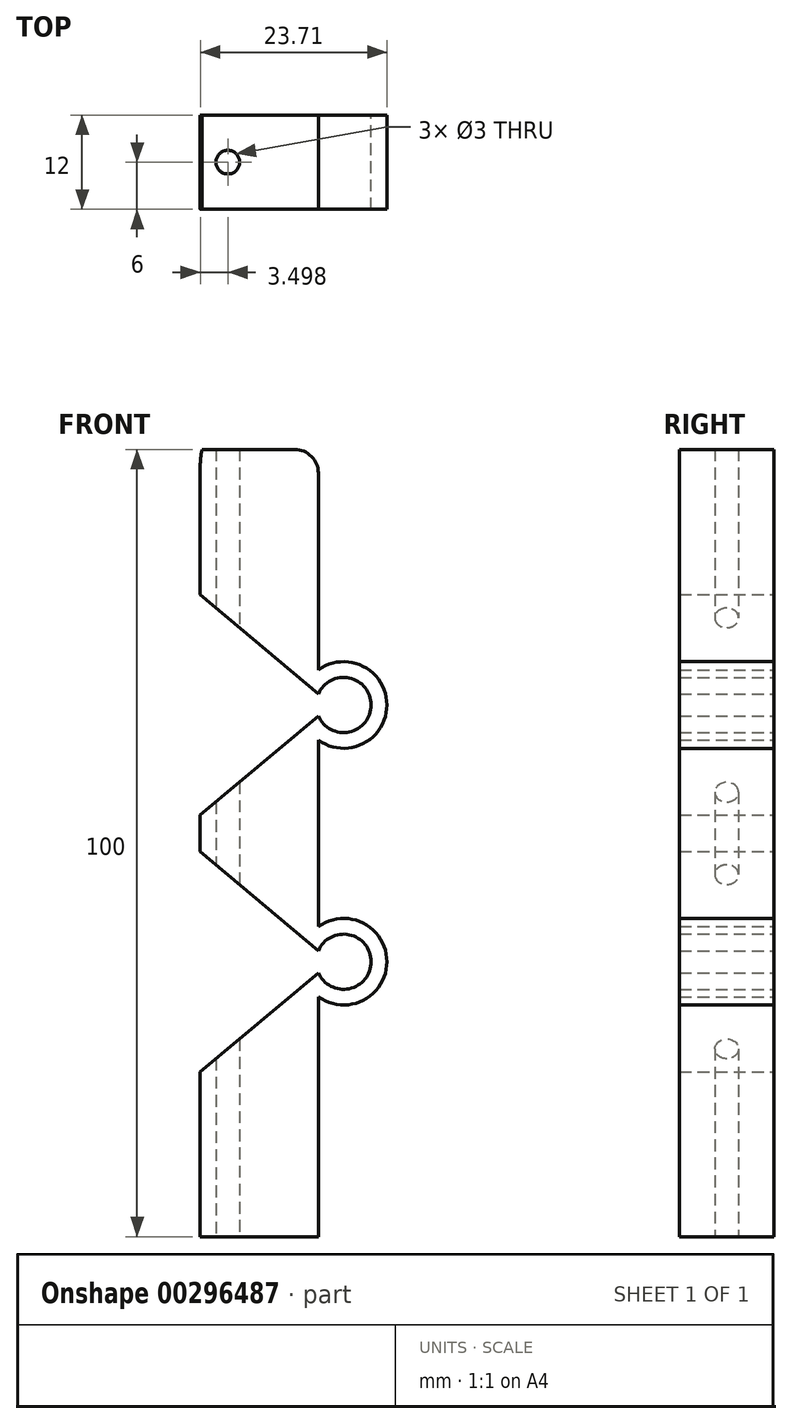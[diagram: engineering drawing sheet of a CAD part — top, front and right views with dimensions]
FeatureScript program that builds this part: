
annotation { "Feature Type Name" : "Feature", "Feature Type Description" : "" }
export const myFeature = defineFeature(function(context is Context, id is Id, definition is map)
    precondition{}
    {
        {
            var Q0;
            Q0=qCreatedBy(makeId("Front.planeOp"),FACE);
            var sketch = newSketch(context, id + "F0", { "sketchPlane" : qUnion([Q0])});
            skLineSegment(sketch, "E0.bottom", {"start": v(-29.07, 0) * mm, "end": v(-44.07, 0) * mm});
            skLineSegment(sketch, "E0.top", {"start": v(-32.07, 100) * mm, "end": v(-43.85, 100) * mm});
            skLineSegment(sketch, "E0.left", {"start": v(-29.07, 0) * mm, "end": v(-29.07, 30.46) * mm});
            skLineSegment(sketch, "E0.right", {"start": v(-44.07, 0) * mm, "end": v(-44.07, 20.92) * mm});
            skLineSegment(sketch, "E1", {"start": v(-29.07, 34.93) * mm, "end": v(-44.07, 34.93) * mm, "construction": true});
            skLineSegment(sketch, "E2", {"start": v(-29.07, 67.54) * mm, "end": v(-44.07, 67.54) * mm, "construction": true});
            skLineSegment(sketch, "E3.trimOffspring", {"start": v(-44.07, 48.93) * mm, "end": v(-44.07, 53.54) * mm});
            skLineSegment(sketch, "E4.trimOffspring", {"start": v(-44.07, 81.55) * mm, "end": v(-44.07, 97.92) * mm});
            skArc(sketch, "E5", {"start": v(-29.36, 35.13) * mm, "mid": v(-29.36, 35.03) * mm, "end": v(-29.36, 34.93) * mm});
            skPoint(sketch, "E5.third.point", {"position": v(-22.36, 34.93) * mm});
            skArc(sketch, "E6", {"start": v(-29.07, 66.14) * mm, "mid": v(-22.36, 67.54) * mm, "end": v(-29.07, 68.94) * mm});
            skPoint(sketch, "E6.third.point", {"position": v(-22.36, 67.54) * mm});
            skArc(sketch, "E7", {"start": v(-29.07, 63.08) * mm, "mid": v(-20.36, 67.54) * mm, "end": v(-29.07, 72.01) * mm});
            skPoint(sketch, "E8.end.orphan", {"position": v(-29.07, 66.14) * mm});
            skPoint(sketch, "E9.MirrorCS.start.orphan", {"position": v(-29.07, 67.54) * mm});
            skLineSegment(sketch, "E10.trimOffspring", {"start": v(-29.07, 72.01) * mm, "end": v(-29.07, 97) * mm});
            skPoint(sketch, "E11.MirrorCS.start.orphan", {"position": v(-29.07, 34.93) * mm});
            skArc(sketch, "E12.trimOffspring", {"start": v(-29.07, 33.53) * mm, "mid": v(-22.36, 34.93) * mm, "end": v(-29.07, 36.33) * mm});
            skLineSegment(sketch, "E13.trimOffspring", {"start": v(-29.07, 39.4) * mm, "end": v(-29.07, 63.08) * mm});
            skArc(sketch, "E14", {"start": v(-29.07, 39.4) * mm, "mid": v(-20.36, 34.93) * mm, "end": v(-29.07, 30.46) * mm});
            skPoint(sketch, "E15.newPointB", {"position": v(-44.07, 100.16) * mm});
            skArc(sketch, "E15.filletArc", {"start": v(-34.07, 107.92) * mm, "mid": v(-41.14, 104.99) * mm, "end": v(-44.07, 97.92) * mm});
            skPoint(sketch, "E16.visualSharp", {"position": v(-29.07, 100) * mm});
            skArc(sketch, "E16.filletArc", {"start": v(-29.07, 97) * mm, "mid": v(-29.95, 99.12) * mm, "end": v(-32.07, 100) * mm});
            skPoint(sketch, "E17.MirrorCS.end.orphan", {"position": v(-44.07, 114.16) * mm});
            skPoint(sketch, "E17.MirrorCS.start.orphan", {"position": v(-29.07, 100.16) * mm});
            skLineSegment(sketch, "E18", {"start": v(-44.07, 48.93) * mm, "end": v(-29.07, 36.33) * mm});
            skLineSegment(sketch, "E19", {"start": v(-44.07, 20.92) * mm, "end": v(-29.07, 33.53) * mm});
            skPoint(sketch, "E20.trimOffspring.start.orphan", {"position": v(-31.07, 36.33) * mm});
            skPoint(sketch, "E21.start.orphan", {"position": v(-31.07, 33.53) * mm});
            skLineSegment(sketch, "E22", {"start": v(-44.07, 81.55) * mm, "end": v(-29.07, 68.94) * mm});
            skLineSegment(sketch, "E23", {"start": v(-29.07, 66.14) * mm, "end": v(-44.07, 53.54) * mm});
            skPoint(sketch, "E24.start.orphan", {"position": v(-31.07, 66.14) * mm});
            skPoint(sketch, "E25.trimOffspring.start.orphan", {"position": v(-31.07, 68.94) * mm});
            skSolve(sketch);
        }
        {
            var Q0;
            Q0=makeQuery(id+"F0.imprint","IMPRINT",FACE,{"disambiguationData":[TD([[makeQuery(id+"F0.imprint","IMPRINT",EDGE,{"derivedFrom":sQuery(id+"F0.wireOp",EDGE,"E0.bottom")}),-1.0]])]});
            extrude(context, id + "F1", {"entities" : qUnion([Q0]), "endBound" : BoundingType.SYMMETRIC, "depth" : 12 * mm});
        }
        {
            var Q0;
            Q0=qCreatedBy(makeId("Top.planeOp"),FACE);
            var sketch = newSketch(context, id + "F2", { "sketchPlane" : qUnion([Q0])});
            skCircle(sketch, "E26", {"center": v(-40.57, 0) * mm, "radius": 1.5 * mm});
            skSolve(sketch);
        }
        {
            var Q0;
            Q0=makeQuery(id+"F2.imprint","IMPRINT",FACE,{"disambiguationData":[TD([[makeQuery(id+"F2.imprint","IMPRINT",EDGE,{"derivedFrom":sQuery(id+"F2.wireOp",EDGE,"E26")}),1.0]])]});
            extrude(context, id + "F3", {"entities" : qUnion([Q0]), "operationType" : NewBodyOperationType.REMOVE, "endBound" : BoundingType.THROUGH_ALL, "depth" : 25 * mm});
        }
    });
